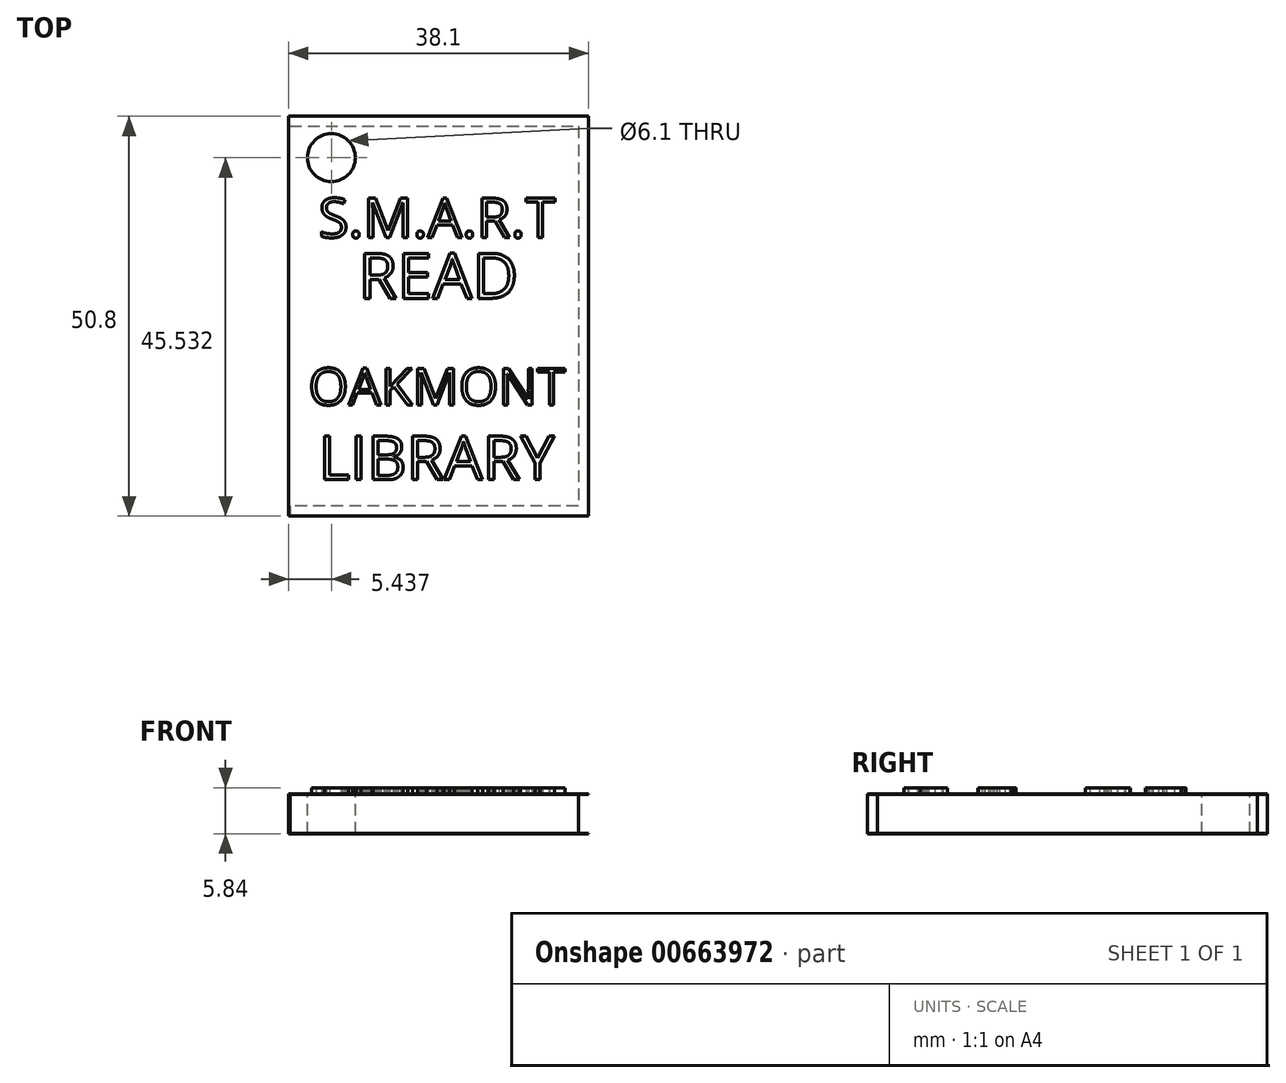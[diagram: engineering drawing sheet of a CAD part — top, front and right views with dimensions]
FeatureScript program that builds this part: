
annotation { "Feature Type Name" : "Feature", "Feature Type Description" : "" }
export const myFeature = defineFeature(function(context is Context, id is Id, definition is map)
    precondition{}
    {
        {
            var Q0;
            Q0=qCreatedBy(makeId("Top.planeOp"),FACE);
            var sketch = newSketch(context, id + "F0", { "sketchPlane" : qUnion([Q0])});
            skLineSegment(sketch, "E0.bottom", {"start": v(-51.28, 36.67) * mm, "end": v(-13.18, 36.67) * mm});
            skLineSegment(sketch, "E0.top", {"start": v(-51.28, -14.13) * mm, "end": v(-13.18, -14.13) * mm});
            skLineSegment(sketch, "E0.left", {"start": v(-51.28, 36.67) * mm, "end": v(-51.28, -14.13) * mm});
            skLineSegment(sketch, "E0.right", {"start": v(-13.18, 36.67) * mm, "end": v(-13.18, -14.13) * mm});
            skSolve(sketch);
        }
        {
            var Q0;
            Q0=makeQuery(id+"F0.imprint","IMPRINT",FACE,{"disambiguationData":[TD([[makeQuery(id+"F0.imprint","IMPRINT",EDGE,{"derivedFrom":sQuery(id+"F0.wireOp",EDGE,"E0.bottom")}),-1.0]])]});
            extrude(context, id + "F1", {"entities" : qUnion([Q0]), "depth" : 5.08 * mm, "offsetDistance" : 25.4 * mm});
        }
        {
            var Q0;
            Q0=makeQuery(id+"F1.opExtrude","CAP_FACE",FACE,{"disambiguationData":[OSD([sQuery(id+"F0.wireOp",EDGE,"E0.bottom"),sQuery(id+"F0.wireOp",EDGE,"E0.top"),sQuery(id+"F0.wireOp",EDGE,"E0.left"),sQuery(id+"F0.wireOp",EDGE,"E0.right")])],"isStart":false});
            var sketch = newSketch(context, id + "F2", { "sketchPlane" : qUnion([Q0])});
            skText(sketch, "E1", { "text": "S.M.A.R.T", "fontName": "OpenSans-Regular.ttf"});
            skText(sketch, "E2", { "text": "READ", "fontName": "OpenSans-Regular.ttf"});
            skLineSegment(sketch, "E3", {"start": v(-32.23, 36.67) * mm, "end": v(-32.23, -17.57) * mm, "construction": true});
            skText(sketch, "E4", { "text": "OAKMONT\n", "fontName": "OpenSans-Regular.ttf"});
            skText(sketch, "E5", { "text": "LIBRARY", "fontName": "OpenSans-Regular.ttf"});
            const initialGuessF2  = {"E1": [-0.04747, 0.02128, 1, 0, 0.00502], "E2": [-0.0424, 0.01354, 1, 0, 0.00576], "E4": [-0.04874, 0, 1, 0, 0.00469], "E5": [-0.04747, -0.0095, 1, 0, 0.00557]};
            skSetInitialGuess(sketch, initialGuessF2);
            skSolve(sketch);
        }
        {
            var Q0;
            Q0 = qSketchRegion(id + "F2", true);
            extrude(context, id + "F3", {"entities" : qUnion([Q0]), "operationType" : NewBodyOperationType.ADD, "depth" : 0.76 * mm, "offsetDistance" : 25.4 * mm});
        }
        {
            var Q0;
            Q0=makeQuery(id+"F1.opExtrude","SWEPT_FACE",FACE,{"disambiguationData":[OSD([sQuery(id+"F0.wireOp",EDGE,"E0.bottom")])]});
            var sketch = newSketch(context, id + "F4", { "sketchPlane" : qUnion([Q0])});
            skLineSegment(sketch, "E6.bottom", {"start": v(51.13, 4.99) * mm, "end": v(13.3, 4.99) * mm});
            skLineSegment(sketch, "E6.top", {"start": v(51.13, 0.06) * mm, "end": v(13.3, 0.06) * mm});
            skLineSegment(sketch, "E6.left", {"start": v(51.13, 4.99) * mm, "end": v(51.13, 0.06) * mm});
            skLineSegment(sketch, "E7", {"start": v(13.3, 4.99) * mm, "end": v(13.18, 4.99) * mm});
            skLineSegment(sketch, "E8", {"start": v(13.3, 0.06) * mm, "end": v(13.18, 0.06) * mm});
            skSolve(sketch);
        }
        {
            var Q0;
            Q0 = qSketchRegion(id + "F4", true);
            var Q1;
            Q1=makeQuery(id+"F4.imprint","IMPRINT",FACE,{"disambiguationData":[TD([[makeQuery(id+"F4.imprint","IMPRINT",EDGE,{"derivedFrom":sQuery(id+"F4.wireOp",EDGE,"E6.bottom")}),1.0]])]});
            extrude(context, id + "F5", {"entities" : qUnion([Q0, Q1]), "operationType" : NewBodyOperationType.REMOVE, "oppositeDirection" : true, "depth" : 1.27 * mm, "offsetDistance" : 25.4 * mm});
        }
        {
            var Q0;
            Q0=makeQuery(id+"F1.opExtrude","SWEPT_FACE",FACE,{"disambiguationData":[OSD([sQuery(id+"F0.wireOp",EDGE,"E0.right")])]});
            var sketch = newSketch(context, id + "F6", { "sketchPlane" : qUnion([Q0])});
            skLineSegment(sketch, "E9", {"start": v(35.4, 4.99) * mm, "end": v(-14.13, 4.99) * mm});
            skLineSegment(sketch, "E10", {"start": v(35.4, 0.06) * mm, "end": v(-14.13, 0.06) * mm});
            skSolve(sketch);
        }
        {
            var Q0;
            Q0 = qSketchRegion(id + "F6", true);
            var Q1;
            {var subQ0=sQuery(id+"F6.wireOp",EDGE,"E9");Q1=makeQuery(id+"F6.imprint","IMPRINT",FACE,{"disambiguationData":[TD([[makeQuery(id+"F6.imprint","IMPRINT",EDGE,{"derivedFrom":subQ0}),1.0]])]});}
            extrude(context, id + "F7", {"entities" : qUnion([Q0, Q1]), "operationType" : NewBodyOperationType.REMOVE, "oppositeDirection" : true, "depth" : 1.27 * mm, "offsetDistance" : 25.4 * mm});
        }
        {
            var Q0;
            Q0=makeQuery(id+"F1.opExtrude","SWEPT_FACE",FACE,{"disambiguationData":[OSD([sQuery(id+"F0.wireOp",EDGE,"E0.top")])]});
            var sketch = newSketch(context, id + "F8", { "sketchPlane" : qUnion([Q0])});
            skLineSegment(sketch, "E11", {"start": v(-14.45, 4.99) * mm, "end": v(-51.1, 4.99) * mm});
            skLineSegment(sketch, "E12", {"start": v(-14.45, 0.06) * mm, "end": v(-51.1, 0.06) * mm});
            skLineSegment(sketch, "E13", {"start": v(-51.1, 4.99) * mm, "end": v(-51.1, 0.06) * mm});
            skPoint(sketch, "E14.orphan", {"position": v(-51.28, 4.99) * mm});
            skPoint(sketch, "E15.orphan", {"position": v(-51.28, 0.06) * mm});
            skSolve(sketch);
        }
        {
            var Q0;
            Q0 = qSketchRegion(id + "F8", true);
            var Q1;
            {var subQ0=sQuery(id+"F8.wireOp",EDGE,"E11");Q1=makeQuery(id+"F8.imprint","IMPRINT",FACE,{"disambiguationData":[TD([[makeQuery(id+"F8.imprint","IMPRINT",EDGE,{"derivedFrom":subQ0}),1.0]])]});}
            extrude(context, id + "F9", {"entities" : qUnion([Q0, Q1]), "operationType" : NewBodyOperationType.REMOVE, "oppositeDirection" : true, "depth" : 1.27 * mm, "offsetDistance" : 25.4 * mm});
        }
        {
            var Q0;
            {var subQ0=sQuery(id+"F0.wireOp",EDGE,"E0.left");var subQ1=sQuery(id+"F0.wireOp",EDGE,"E0.bottom");var subQ2=sQuery(id+"F0.wireOp",EDGE,"E0.right");var subQ3=sQuery(id+"F0.wireOp",EDGE,"E0.top");Q0=makeQuery(id+"F3.boolean.opBoolean","SPLIT",FACE,{"disambiguationData":[TD([makeQuery(id+"F1.opExtrude","SWEPT_FACE",FACE,{"disambiguationData":[OSD([subQ1])]})])],"derivedFrom":makeQuery(id+"F1.opExtrude","CAP_FACE",FACE,{"disambiguationData":[OSD([subQ1,subQ3,subQ0,subQ2])],"isStart":false})});}
            var sketch = newSketch(context, id + "F10", { "sketchPlane" : qUnion([Q0])});
            skCircle(sketch, "E16", {"center": v(-45.84, 31.4) * mm, "radius": 3.05 * mm});
            skSolve(sketch);
        }
        {
            var Q0;
            Q0=makeQuery(id+"F10.imprint","IMPRINT",FACE,{"disambiguationData":[TD([[makeQuery(id+"F10.imprint","IMPRINT",EDGE,{"derivedFrom":sQuery(id+"F10.wireOp",EDGE,"E16")}),1.0]])]});
            extrude(context, id + "F11", {"entities" : qUnion([Q0]), "operationType" : NewBodyOperationType.REMOVE, "oppositeDirection" : true, "depth" : 127 * mm, "offsetDistance" : 25.4 * mm});
        }
    });
